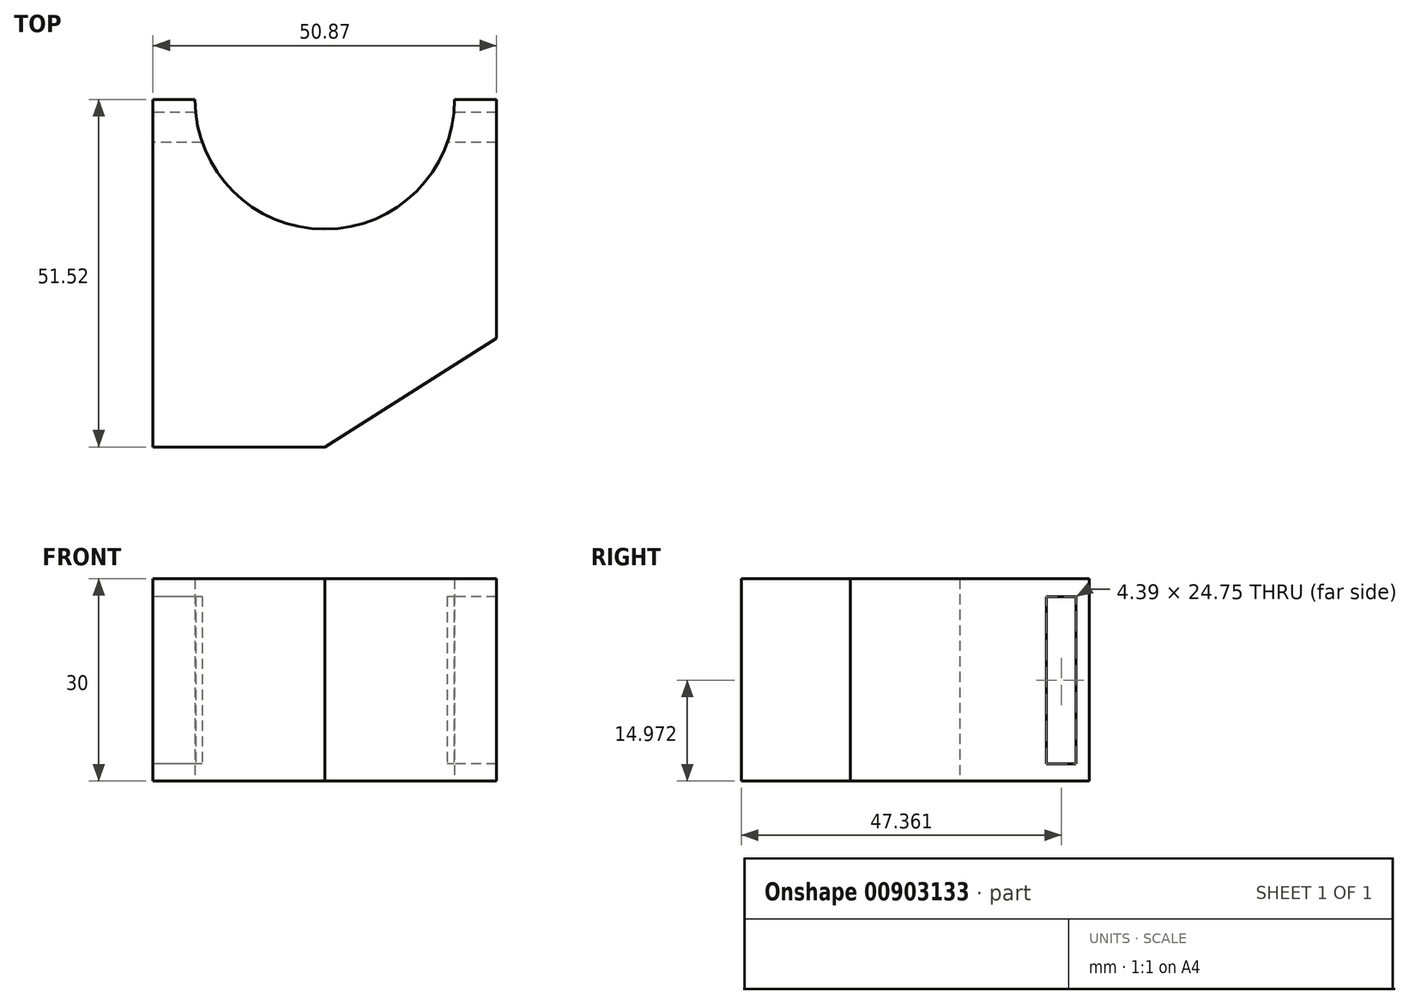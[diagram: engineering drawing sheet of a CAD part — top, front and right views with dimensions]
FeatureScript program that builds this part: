
annotation { "Feature Type Name" : "Feature", "Feature Type Description" : "" }
export const myFeature = defineFeature(function(context is Context, id is Id, definition is map)
    precondition{}
    {
        {
            var Q0;
            Q0=qCreatedBy(makeId("Top.planeOp"),FACE);
            var sketch = newSketch(context, id + "F0", { "sketchPlane" : qUnion([Q0])});
            skLineSegment(sketch, "E0.bottom", {"start": v(0, 0) * mm, "end": v(-50.87, 0) * mm});
            skLineSegment(sketch, "E0.top", {"start": v(-25.44, -32.3) * mm, "end": v(-50.87, -32.3) * mm});
            skLineSegment(sketch, "E0.left", {"start": v(0, 0) * mm, "end": v(0, -16.15) * mm});
            skLineSegment(sketch, "E0.right", {"start": v(-50.87, 0) * mm, "end": v(-50.87, -32.3) * mm});
            skLineSegment(sketch, "E1", {"start": v(-25.44, -32.3) * mm, "end": v(0, -16.15) * mm});
            skPoint(sketch, "E2.orphan", {"position": v(0, -32.3) * mm});
            skArc(sketch, "E3", {"start": v(-44.66, 19.23) * mm, "mid": v(-25.44, 0) * mm, "end": v(-6.21, 19.23) * mm});
            skLineSegment(sketch, "E4", {"start": v(-50.87, 0) * mm, "end": v(-50.87, 19.23) * mm});
            skLineSegment(sketch, "E5", {"start": v(-50.87, 19.23) * mm, "end": v(-44.66, 19.23) * mm});
            skLineSegment(sketch, "E6", {"start": v(0, 19.23) * mm, "end": v(0, 0) * mm});
            skLineSegment(sketch, "E7.trimOffspring", {"start": v(-6.21, 19.23) * mm, "end": v(0, 19.23) * mm});
            skSolve(sketch);
        }
        {
            var Q0;
            Q0=makeQuery(id+"F0.imprint","IMPRINT",FACE,{"disambiguationData":[TD([[makeQuery(id+"F0.imprint","IMPRINT",EDGE,{"derivedFrom":sQuery(id+"F0.wireOp",EDGE,"E0.top")}),-1.0]])]});
            var Q1;
            {var subQ0=sQuery(id+"F0.wireOp",EDGE,"E6");Q1=makeQuery(id+"F0.imprint","IMPRINT",FACE,{"disambiguationData":[TD([[makeQuery(id+"F0.imprint","IMPRINT",EDGE,{"derivedFrom":subQ0}),-1.0]])]});}
            var Q2;
            {var subQ0=sQuery(id+"F0.wireOp",EDGE,"E4");Q2=makeQuery(id+"F0.imprint","IMPRINT",FACE,{"disambiguationData":[TD([[makeQuery(id+"F0.imprint","IMPRINT",EDGE,{"derivedFrom":subQ0}),-1.0]])]});}
            extrude(context, id + "F1", {"entities" : qUnion([Q0, Q1, Q2]), "depth" : 30 * mm, "offsetDistance" : 25 * mm});
        }
        {
            var Q0;
            Q0=makeQuery(id+"F1.opExtrude","SWEPT_FACE",FACE,{"disambiguationData":[OSD([sQuery(id+"F0.wireOp",EDGE,"E0.right"),sQuery(id+"F0.wireOp",EDGE,"E4")])]});
            var sketch = newSketch(context, id + "F2", { "sketchPlane" : qUnion([Q0])});
            skLineSegment(sketch, "E8.bottom", {"start": v(-17.27, 27.35) * mm, "end": v(-12.88, 27.35) * mm});
            skLineSegment(sketch, "E8.top", {"start": v(-17.27, 2.6) * mm, "end": v(-12.88, 2.6) * mm});
            skLineSegment(sketch, "E8.left", {"start": v(-17.27, 27.35) * mm, "end": v(-17.27, 2.6) * mm});
            skLineSegment(sketch, "E8.right", {"start": v(-12.88, 27.35) * mm, "end": v(-12.88, 2.6) * mm});
            skSolve(sketch);
        }
        {
            var Q0;
            Q0=makeQuery(id+"F2.imprint","IMPRINT",FACE,{"disambiguationData":[TD([[makeQuery(id+"F2.imprint","IMPRINT",EDGE,{"derivedFrom":sQuery(id+"F2.wireOp",EDGE,"E8.bottom")}),-1.0]])]});
            extrude(context, id + "F3", {"entities" : qUnion([Q0]), "operationType" : NewBodyOperationType.REMOVE, "endBound" : BoundingType.THROUGH_ALL, "oppositeDirection" : true, "depth" : 25 * mm, "offsetDistance" : 25 * mm});
        }
    });
